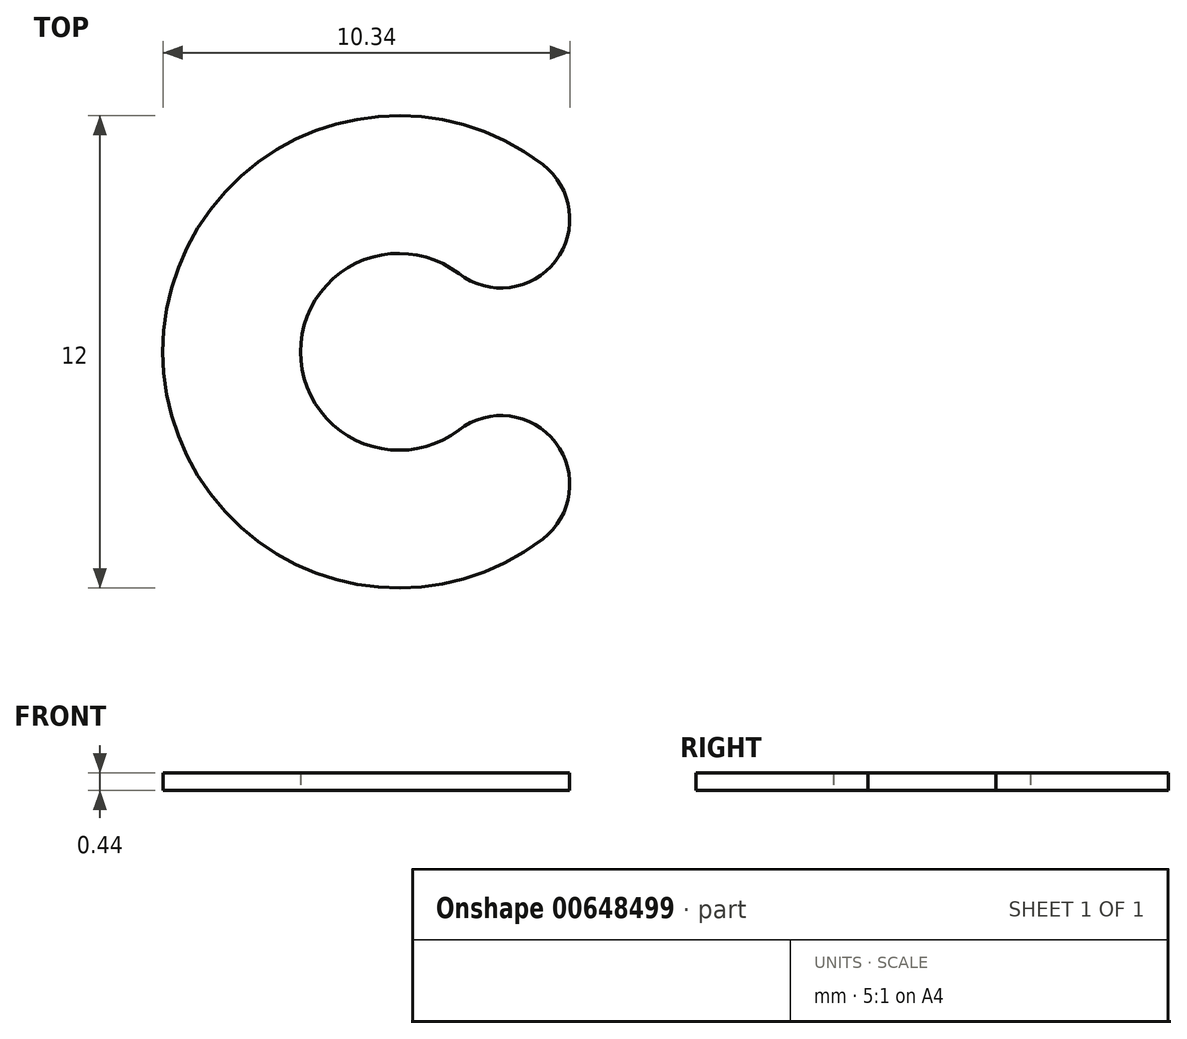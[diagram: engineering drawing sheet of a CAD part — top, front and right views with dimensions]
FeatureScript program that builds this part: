
annotation { "Feature Type Name" : "Feature", "Feature Type Description" : "" }
export const myFeature = defineFeature(function(context is Context, id is Id, definition is map)
    precondition{}
    {
        {
            var Q0;
            Q0=qCreatedBy(makeId("Top.planeOp"),FACE);
            var sketch = newSketch(context, id + "F0", { "sketchPlane" : qUnion([Q0])});
            skArc(sketch, "E0", {"start": v(1.52, 1.98) * mm, "mid": v(-2.5, 0) * mm, "end": v(1.52, -1.98) * mm});
            skArc(sketch, "E1", {"start": v(3.65, 4.76) * mm, "mid": v(-6, 0) * mm, "end": v(3.65, -4.76) * mm});
            skArc(sketch, "E2", {"start": v(1.52, 1.98) * mm, "mid": v(3.98, 2.3) * mm, "end": v(3.65, 4.76) * mm});
            skArc(sketch, "E3.MirrorCS", {"start": v(1.52, -1.98) * mm, "mid": v(3.98, -2.3) * mm, "end": v(3.65, -4.76) * mm});
            skLineSegment(sketch, "E4", {"start": v(2.59, 3.37) * mm, "end": v(0, 0) * mm, "construction": true});
            skLineSegment(sketch, "E5", {"start": v(2.59, -3.37) * mm, "end": v(0, 0) * mm, "construction": true});
            skSolve(sketch);
        }
        {
            var Q0;
            Q0=makeQuery(id+"F0.imprint","IMPRINT",FACE,{"disambiguationData":[TD([[makeQuery(id+"F0.imprint","IMPRINT",EDGE,{"derivedFrom":sQuery(id+"F0.wireOp",EDGE,"E0")}),-1.0]])]});
            extrude(context, id + "F1", {"entities" : qUnion([Q0]), "depth" : 0.44 * mm, "offsetDistance" : 25 * mm});
        }
    });
